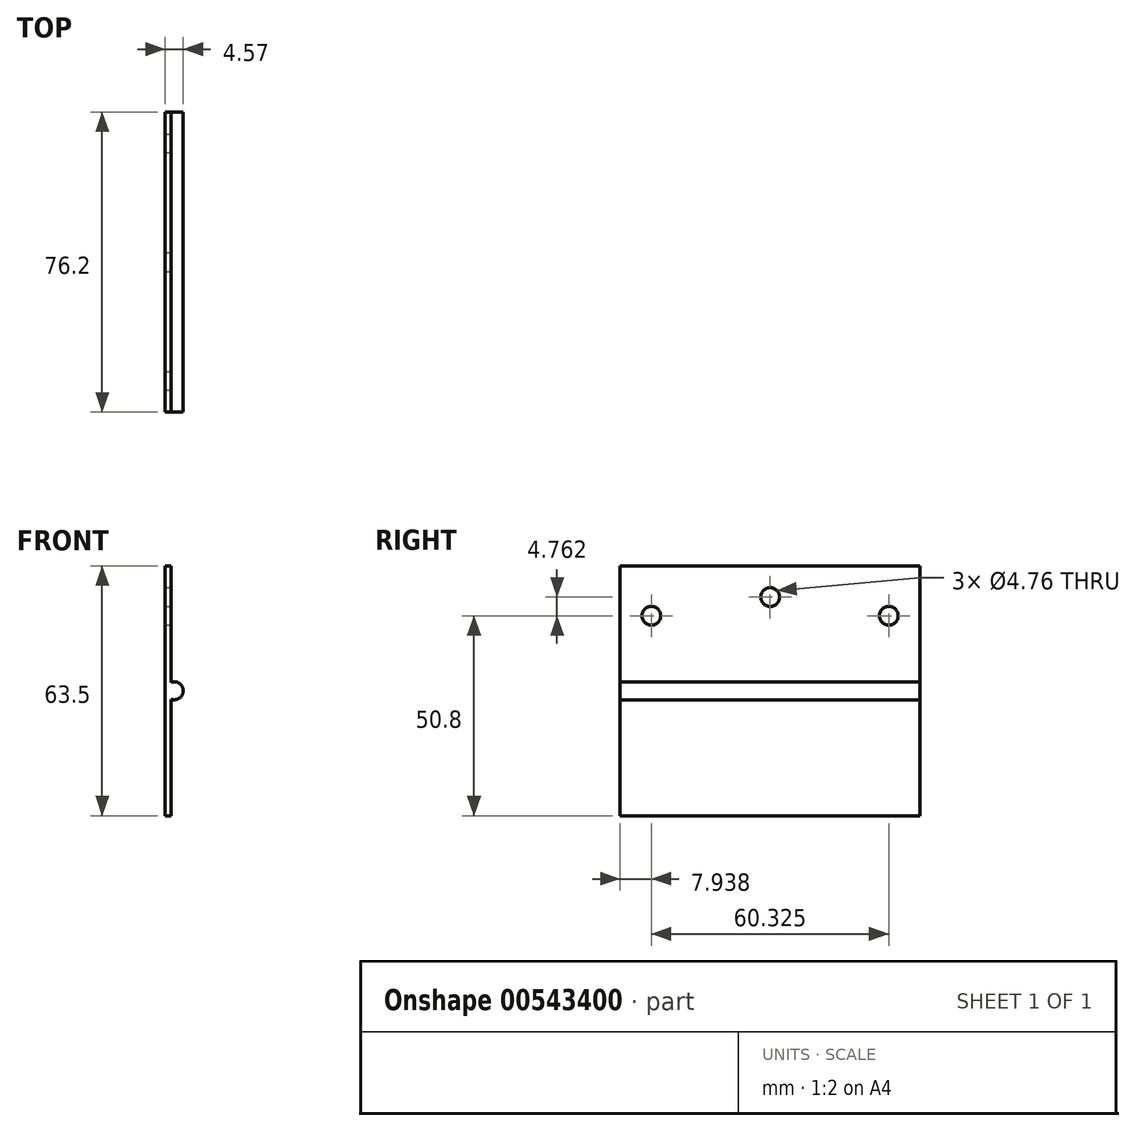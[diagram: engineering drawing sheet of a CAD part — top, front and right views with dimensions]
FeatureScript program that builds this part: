
annotation { "Feature Type Name" : "Feature", "Feature Type Description" : "" }
export const myFeature = defineFeature(function(context is Context, id is Id, definition is map)
    precondition{}
    {
        {
            var Q0;
            Q0=qCreatedBy(makeId("Right.planeOp"),FACE);
            var sketch = newSketch(context, id + "F0", { "sketchPlane" : qUnion([Q0])});
            skLineSegment(sketch, "E0.bottom", {"start": v(-38.1, 31.75) * mm, "end": v(38.1, 31.75) * mm});
            skLineSegment(sketch, "E0.top", {"start": v(-38.1, -31.75) * mm, "end": v(38.1, -31.75) * mm});
            skLineSegment(sketch, "E0.left", {"start": v(-38.1, 31.75) * mm, "end": v(-38.1, -31.75) * mm});
            skLineSegment(sketch, "E0.right", {"start": v(38.1, 31.75) * mm, "end": v(38.1, -31.75) * mm});
            skPoint(sketch, "E0.middle", {"position": v(0, 0) * mm});
            skSolve(sketch);
        }
        {
            var Q0;
            Q0=makeQuery(id+"F0.imprint","IMPRINT",FACE,{"disambiguationData":[TD([[makeQuery(id+"F0.imprint","IMPRINT",EDGE,{"derivedFrom":sQuery(id+"F0.wireOp",EDGE,"E0.bottom")}),-1.0]])]});
            extrude(context, id + "F1", {"entities" : qUnion([Q0]), "depth" : 1.52 * mm, "offsetDistance" : 25.4 * mm});
        }
        {
            var Q0;
            Q0=makeQuery(id+"F1.opExtrude","SWEPT_FACE",FACE,{"disambiguationData":[OSD([sQuery(id+"F0.wireOp",EDGE,"E0.left")])]});
            var sketch = newSketch(context, id + "F2", { "sketchPlane" : qUnion([Q0])});
            skCircle(sketch, "E1", {"center": v(2.29, 0) * mm, "radius": 2.29 * mm});
            skSolve(sketch);
        }
        {
            var Q0;
            {var subQ0=sQuery(id+"F2.wireOp",EDGE,"E1");var subQ1=makeQuery(id+"F1.opExtrude","CAP_EDGE",EDGE,{"disambiguationData":[OSD([sQuery(id+"F0.wireOp",EDGE,"E0.left")])],"isStart":false});var subQ2=makeQuery(id+"F2.imprint","INTERSECT",VERTEX,{"disambiguationData":[OD(0.0)],"derivedFrom":[subQ1,subQ0]});Q0=makeQuery(id+"F2.imprint","IMPRINT",FACE,{"disambiguationData":[TD([[makeQuery(id+"F2.imprint","IMPRINT",EDGE,{"disambiguationData":[TD([[subQ2,1.0]])],"derivedFrom":subQ0}),1.0]])]});}
            var Q1;
            Q1=makeQuery(id+"F1.opExtrude","SWEPT_FACE",FACE,{"disambiguationData":[OSD([sQuery(id+"F0.wireOp",EDGE,"E0.right")])]});
            extrude(context, id + "F3", {"entities" : qUnion([Q0]), "operationType" : NewBodyOperationType.ADD, "endBound" : BoundingType.UP_TO_SURFACE, "oppositeDirection" : true, "depth" : 25.4 * mm, "endBoundEntityFace" : qUnion([Q1]), "offsetDistance" : 25.4 * mm});
        }
        {
            var Q0;
            {var subQ0=sQuery(id+"F0.wireOp",EDGE,"E0.right");var subQ1=sQuery(id+"F0.wireOp",EDGE,"E0.left");var subQ2=sQuery(id+"F0.wireOp",EDGE,"E0.bottom");Q0=makeQuery(id+"F3.boolean.opBoolean","SPLIT",FACE,{"disambiguationData":[TD([makeQuery(id+"F1.opExtrude","SWEPT_FACE",FACE,{"disambiguationData":[OSD([subQ2])]})])],"derivedFrom":makeQuery(id+"F1.opExtrude","CAP_FACE",FACE,{"disambiguationData":[OSD([subQ2,sQuery(id+"F0.wireOp",EDGE,"E0.top"),subQ1,subQ0])],"isStart":false})});}
            var sketch = newSketch(context, id + "F4", { "sketchPlane" : qUnion([Q0])});
            skPoint(sketch, "E2", {"position": v(0, 23.81) * mm});
            skPoint(sketch, "E3", {"position": v(-30.16, 19.05) * mm});
            skPoint(sketch, "E4", {"position": v(30.16, 19.05) * mm});
            skLineSegment(sketch, "E5", {"start": v(0, 31.75) * mm, "end": v(0, -39.11) * mm, "construction": true});
            skPoint(sketch, "E5.endSnap0", {"position": v(0, 31.75) * mm});
            skSolve(sketch);
        }
        {
            var Q0;
            Q0=sQuery(id+"F4.wireOp",VERTEX,"E3");
            var Q1;
            Q1=sQuery(id+"F4.wireOp",VERTEX,"E2");
            var Q2;
            Q2=sQuery(id+"F4.wireOp",VERTEX,"E4");
            var Q3;
            Q3=makeQuery(id+"F1.opExtrude","SWEPT_BODY",BODY,{"disambiguationData":[OSD([sQuery(id+"F0.wireOp",EDGE,"E0.bottom"),sQuery(id+"F0.wireOp",EDGE,"E0.top"),sQuery(id+"F0.wireOp",EDGE,"E0.left"),sQuery(id+"F0.wireOp",EDGE,"E0.right")])]});
            hole(context, id + "F5", {"style" : HoleStyle.SIMPLE, "endStyle" : HoleEndStyle.THROUGH, "holeDiameter" : 4.76 * mm, "majorDiameter" : 6.35 * mm, "isTappedThrough" : true, "tappedDepth" : 12.7 * mm, "tapClearance" : 3, "startFromSketch" : true, "locations" : qUnion([Q0, Q1, Q2]), "scope" : qUnion([Q3])});
        }
    });
